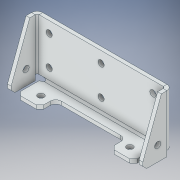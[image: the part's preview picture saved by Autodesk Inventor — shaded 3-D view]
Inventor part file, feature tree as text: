
AUTODESK INVENTOR PART (.ipt)
format: ipt  version: 2018 (Build 220112000, 112)  size: 192,512 bytes
history: native  units: in
note: dims shown in document units (in); Inventor stores cm internally (conversion verified against a paired STEP export)
features: other x1, chamfer x1
ambient origin geometry x8: Origin, YZ Plane, XZ Plane, XY Plane, X Axis, Y Axis, Z Axis, Center Point
bodies: Solid1 (feature_tree)
feature tree (2):
  other  "am-3961 AM14U4 2019 Front Bumper Bracket1"
  chamfer  "Chamfer3"  [1 undecoded]
note: 1 required parameter value undecoded (feature->parameter linkage not recoverable at this tier; creation-order binding heuristic only, values carry confidence <= 0.55)
